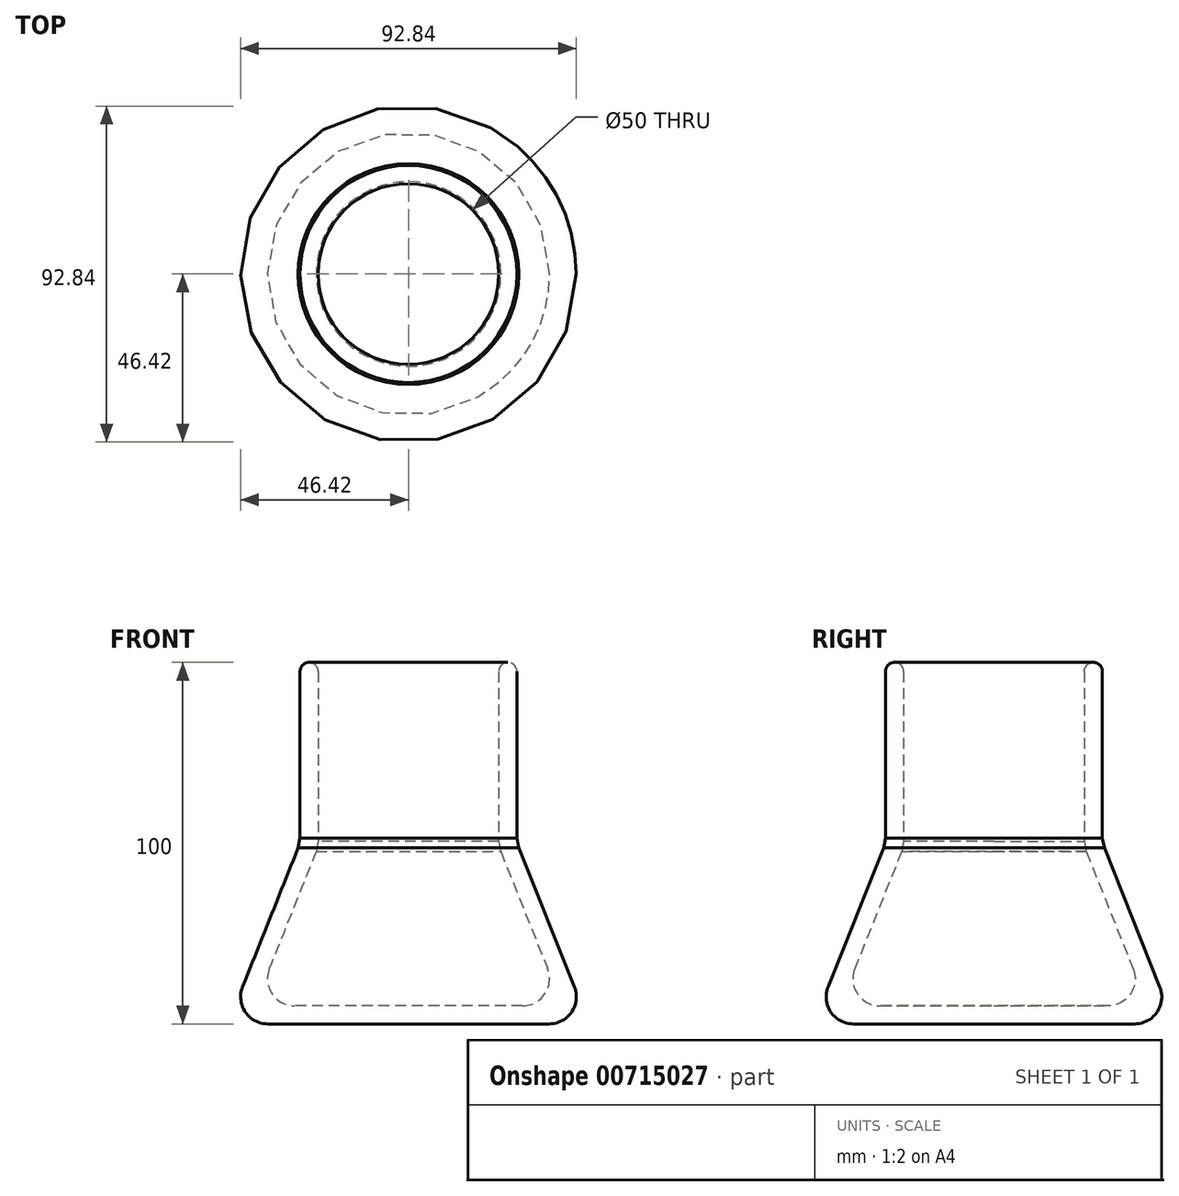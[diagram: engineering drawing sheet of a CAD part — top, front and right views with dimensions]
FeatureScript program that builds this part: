
annotation { "Feature Type Name" : "Feature", "Feature Type Description" : "" }
export const myFeature = defineFeature(function(context is Context, id is Id, definition is map)
    precondition{}
    {
        {
            var Q0;
            Q0=qCreatedBy(makeId("Top.planeOp"),FACE);
            var sketch = newSketch(context, id + "F0", { "sketchPlane" : qUnion([Q0])});
            skCircle(sketch, "E0", {"center": v(0, 0) * mm, "radius": 50 * mm});
            skSolve(sketch);
        }
        {
            var Q0;
            Q0=makeQuery(id+"F0.imprint","IMPRINT",FACE,{"disambiguationData":[TD([[makeQuery(id+"F0.imprint","IMPRINT",EDGE,{"derivedFrom":sQuery(id+"F0.wireOp",EDGE,"E0")}),1.0]])]});
            cPlane(context, id + "F1", {"entities" : qUnion([Q0]), "cplaneType" : CPlaneType.OFFSET, "offset" : 50 * mm, "width" : 150 * mm, "height" : 150 * mm});
        }
        {
            var Q0;
            Q0=qCreatedBy(id+"F1.planeOp",FACE);
            var sketch = newSketch(context, id + "F2", { "sketchPlane" : qUnion([Q0])});
            skCircle(sketch, "E1", {"center": v(0, 0) * mm, "radius": 30 * mm});
            skSolve(sketch);
        }
        {
            var Q0;
            Q0=makeQuery(id+"F0.imprint","IMPRINT",FACE,{"disambiguationData":[TD([[makeQuery(id+"F0.imprint","IMPRINT",EDGE,{"derivedFrom":sQuery(id+"F0.wireOp",EDGE,"E0")}),1.0]])]});
            var Q1;
            Q1=makeQuery(id+"F2.imprint","IMPRINT",FACE,{"disambiguationData":[TD([[makeQuery(id+"F2.imprint","IMPRINT",EDGE,{"derivedFrom":sQuery(id+"F2.wireOp",EDGE,"E1")}),1.0]])]});
            loft(context, id + "F3", {"sheetProfilesArray" : [{ "sheetProfileEntities" : qUnion([Q0]) }, { "sheetProfileEntities" : qUnion([Q1]) }]});
        }
        {
            var Q0;
            Q0=makeQuery(id+"F3.opLoft","CAP_FACE",FACE,{"disambiguationData":[OSD([makeQuery(id+"F2.imprint","IMPRINT",FACE,{"disambiguationData":[TD([[makeQuery(id+"F2.imprint","IMPRINT",EDGE,{"derivedFrom":sQuery(id+"F2.wireOp",EDGE,"E1")}),1.0]])]})])],"isStart":true});
            extrude(context, id + "F4", {"entities" : qUnion([Q0]), "operationType" : NewBodyOperationType.ADD, "depth" : 50 * mm, "offsetDistance" : 25 * mm});
        }
        {
            var Q0;
            Q0=makeQuery(id+"F4.opExtrude","CAP_FACE",FACE,{"disambiguationData":[OSD([makeQuery(id+"F2.imprint","IMPRINT",FACE,{"disambiguationData":[TD([[makeQuery(id+"F2.imprint","IMPRINT",EDGE,{"derivedFrom":sQuery(id+"F2.wireOp",EDGE,"E1")}),1.0]])]})])],"isStart":false});
            shell(context, id + "F5", {"entities" : qUnion([Q0]), "thickness" : 5 * mm});
        }
        {
            var Q0;
            Q0=makeQuery(id+"F4.opExtrude","CAP_EDGE",EDGE,{"disambiguationData":[OSD([sQuery(id+"F2.wireOp",EDGE,"E1")])],"isStart":false});
            var Q1;
            {var subQ0=sQuery(id+"F2.wireOp",EDGE,"E1");Q1=makeQuery(id+"F5.opShell","OFFSET_EDGE",EDGE,{"disambiguationData":[OSD([subQ0]),TDD([makeQuery(id+"F4.opExtrude","CAP_EDGE",EDGE,{"disambiguationData":[OSD([subQ0])],"isStart":false})])]});}
            fillet(context, id + "F6", {"entities" : qUnion([Q0, Q1]), "radius" : 2.5 * mm, "tangentPropagation" : true, "allowEdgeOverflow" : false});
        }
        {
            var Q0;
            Q0=makeQuery(id+"F3.opLoft","CAP_FACE",FACE,{"disambiguationData":[OSD([makeQuery(id+"F0.imprint","IMPRINT",FACE,{"disambiguationData":[TD([[makeQuery(id+"F0.imprint","IMPRINT",EDGE,{"derivedFrom":sQuery(id+"F0.wireOp",EDGE,"E0")}),1.0]])]})])],"isStart":true});
            var Q1;
            Q1=makeQuery(id+"F5.opShell","OFFSET_EDGE",EDGE,{"disambiguationData":[OSD([sQuery(id+"F0.wireOp",EDGE,"E0")])]});
            fillet(context, id + "F7", {"entities" : qUnion([Q0, Q1]), "radius" : 7.5 * mm, "tangentPropagation" : true, "allowEdgeOverflow" : false});
        }
        {
            var Q0;
            {var subQ0=sQuery(id+"F2.wireOp",EDGE,"E1");Q0=makeQuery(id+"F4.boolean.opBoolean","MERGE",EDGE,{"derivedFrom":[makeQuery(id+"F3.opLoft","MID_CAP_EDGE",EDGE,{"disambiguationData":[OSD([subQ0])],"capPos":1.0}),makeQuery(id+"F4.opExtrude","CAP_EDGE",EDGE,{"disambiguationData":[OSD([subQ0])],"isStart":true})]});}
            var Q1;
            {var subQ0=sQuery(id+"F2.wireOp",EDGE,"E1");Q1=makeQuery(id+"F5.opShell","OFFSET_EDGE",EDGE,{"disambiguationData":[OSD([subQ0]),TDD([makeQuery(id+"F4.boolean.opBoolean","MERGE",EDGE,{"derivedFrom":[makeQuery(id+"F3.opLoft","MID_CAP_EDGE",EDGE,{"disambiguationData":[OSD([subQ0])],"capPos":1.0}),makeQuery(id+"F4.opExtrude","CAP_EDGE",EDGE,{"disambiguationData":[OSD([subQ0])],"isStart":true})]})])]});}
            chamfer(context, id + "F8", {"entities" : qUnion([Q0, Q1]), "width" : 7.5 * mm, "tangentPropagation" : true});
        }
    });
